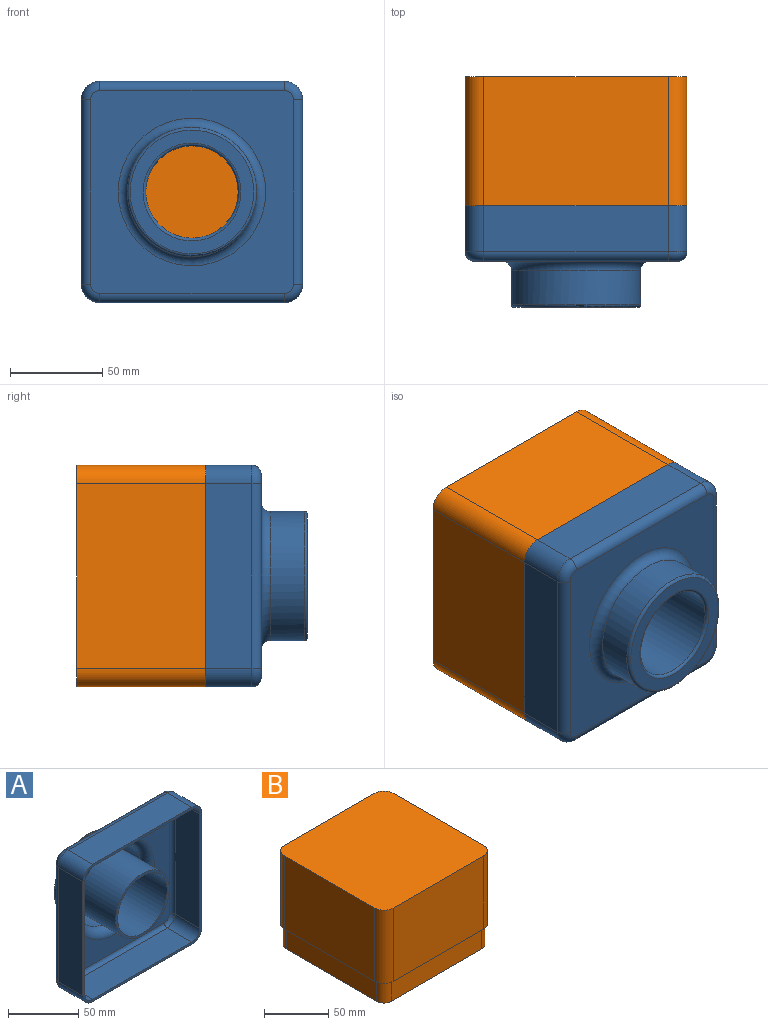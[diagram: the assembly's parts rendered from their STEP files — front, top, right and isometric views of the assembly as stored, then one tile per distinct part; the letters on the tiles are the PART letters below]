
ASSEMBLY  parts=2 mates=1
PART A: 46 faces, bbox 121.6x55x121.6 mm
  f0: plane 120x120mm, normal (0,-1,0), area 913.1mm2, adj f1,f3,f5,f6,f10,f12,f15,f21
  f1: plane 100x25mm, normal (-1,0,0), area 2500mm2, adj f0,f12,f18,f21
  f2: plane 54x54mm, normal (0,-1,0), area 326.7mm2, adj f9,f32
  f3: plane 100x25mm, normal (1,0,0), area 2500mm2, adj f0,f10,f14,f15
  f4: plane 110x110mm, normal (0,1,0), area 7052mm2, adj f11,f13,f14,f16,f17,f18,f19,f20
  f5: plane 100x25mm, normal (0,0,1), area 2500mm2, adj f0,f15,f19,f21
  f6: plane 100x25mm, normal (0,0,-1), area 2500mm2, adj f0,f10,f12,f13
  f7: cylinder r=35mm len=70mm, axis (0,-1,0), area 4068.4mm2, adj f22,f23
  f8: plane 67x67mm, normal (0,1,0), area 1319.5mm2, adj f23,f24
  f9: cylinder r=25mm len=53.5mm, axis (0,1,0), area 8403.8mm2, adj f2,f24
  f10: cylinder r=10mm len=25mm, axis (0,1,0), area 392.7mm2, adj f0,f3,f6,f11
  f11: torus R=5mm, axis (0,-1,0), area 101mm2, adj f4,f10,f13,f14
  f12: cylinder r=10mm len=25mm, axis (0,-1,0), area 392.7mm2, adj f0,f1,f6,f16
  f13: cylinder r=5mm len=100mm, axis (-1,0,0), area 785.4mm2, adj f4,f6,f11,f16
  f14: cylinder r=5mm len=100mm, axis (0,0,-1), area 785.4mm2, adj f3,f4,f11,f17
  f15: cylinder r=10mm len=25mm, axis (0,-1,0), area 392.7mm2, adj f0,f3,f5,f17
  f16: torus R=5mm, axis (0,-1,0), area 101mm2, adj f4,f12,f13,f18
  f17: torus R=5mm, axis (0,-1,0), area 101mm2, adj f4,f14,f15,f19
  f18: cylinder r=5mm len=100mm, axis (0,0,-1), area 785.4mm2, adj f1,f4,f16,f20
  f19: cylinder r=5mm len=100mm, axis (1,0,0), area 785.4mm2, adj f4,f5,f17,f20
  f20: torus R=5mm, axis (0,-1,0), area 101mm2, adj f4,f18,f19,f21
  f21: cylinder r=10mm len=25mm, axis (0,1,0), area 392.7mm2, adj f0,f1,f5,f20
  f22: torus R=40mm, axis (0,-1,0), area 1816.8mm2, adj f4,f7
  f23: torus R=33.5mm, axis (0,1,0), area 510.1mm2, adj f7,f8
  f24: torus R=26.5mm, axis (0,1,0), area 378.2mm2, adj f8,f9
  f25: plane 100x25mm, normal (1,0,0), area 2500mm2, adj f0,f35,f41,f44
  f26: plane 100x25mm, normal (-1,0,0), area 2500mm2, adj f0,f33,f37,f38
  f27: plane 110x110mm, normal (0,-1,0), area 7052mm2, adj f34,f36,f37,f39,f40,f41,f42,f43
  f28: plane 100x25mm, normal (0,0,-1), area 2500mm2, adj f0,f38,f42,f44
  f29: plane 100x25mm, normal (0,0,1), area 2500mm2, adj f0,f33,f35,f36
  f30: cylinder r=33mm len=66mm, axis (0,-1,0), area 3732.2mm2, adj f31,f45
  f31: plane 66x66mm, normal (0,-1,0), area 1131mm2, adj f30,f32
  f32: cylinder r=27mm len=54mm, axis (0,1,0), area 8991.2mm2, adj f2,f31
  f33: cylinder r=8mm len=25mm, axis (0,1,0), area 314.2mm2, adj f0,f26,f29,f34
  f34: torus R=5mm, axis (0,-1,0), area 51.1mm2, adj f27,f33,f36,f37
  f35: cylinder r=8mm len=25mm, axis (0,-1,0), area 314.2mm2, adj f0,f25,f29,f39
  f36: cylinder r=3mm len=100mm, axis (-1,0,0), area 471.2mm2, adj f27,f29,f34,f39
  f37: cylinder r=3mm len=100mm, axis (0,0,-1), area 471.2mm2, adj f26,f27,f34,f40
  f38: cylinder r=8mm len=25mm, axis (0,-1,0), area 314.2mm2, adj f0,f26,f28,f40
  f39: torus R=5mm, axis (0,-1,0), area 51.1mm2, adj f27,f35,f36,f41
  f40: torus R=5mm, axis (0,-1,0), area 51.1mm2, adj f27,f37,f38,f42
  f41: cylinder r=3mm len=100mm, axis (0,0,-1), area 471.2mm2, adj f25,f27,f39,f43
  f42: cylinder r=3mm len=100mm, axis (1,0,0), area 471.2mm2, adj f27,f28,f40,f43
  f43: torus R=5mm, axis (0,-1,0), area 51.1mm2, adj f27,f41,f42,f44
  f44: cylinder r=8mm len=25mm, axis (0,1,0), area 314.2mm2, adj f0,f25,f28,f43
  f45: torus R=40mm, axis (0,-1,0), area 2455.6mm2, adj f27,f30
PART B: 28 faces, bbox 120x120x90 mm
  f0: plane 116.19x116.19mm, normal (0,0,-1), area 930.8mm2, adj f1,f2,f3,f4,f6,f7,f8,f9
  f1: plane 100x86mm, normal (0,-1,0), area 8600mm2, adj f0,f5,f6,f9
  f2: plane 100x86mm, normal (1,0,0), area 8600mm2, adj f0,f5,f6,f7
  f3: plane 100x86mm, normal (0,1,0), area 8600mm2, adj f0,f5,f7,f8
  f4: plane 100x86mm, normal (-1,0,0), area 8600mm2, adj f0,f5,f8,f9
  f5: plane 112x112mm, normal (0,0,-1), area 12513.1mm2, adj f1,f2,f3,f4,f6,f7,f8,f9
  f6: cylinder r=6mm len=86mm, axis (0,0,1), area 810.5mm2, adj f0,f1,f2,f5
  f7: cylinder r=6mm len=86mm, axis (0,0,-1), area 810.5mm2, adj f0,f2,f3,f5
  f8: cylinder r=6mm len=86mm, axis (0,0,1), area 810.5mm2, adj f0,f3,f4,f5
  f9: cylinder r=6mm len=86mm, axis (0,0,-1), area 810.5mm2, adj f0,f1,f4,f5
  f10: cylinder r=8.1mm len=20mm, axis (0,0,-1), area 254.3mm2, adj f0,f11,f17,f18
  f11: plane 100x20mm, normal (-1,0,0), area 2000mm2, adj f0,f10,f12,f18
  f12: cylinder r=8.1mm len=20mm, axis (0,0,-1), area 254.3mm2, adj f0,f11,f13,f18
  f13: plane 100x20mm, normal (0,-1,0), area 2000mm2, adj f0,f12,f14,f18
  f14: cylinder r=8.1mm len=20mm, axis (0,0,-1), area 254.3mm2, adj f0,f13,f15,f18
  f15: plane 100x20mm, normal (1,0,0), area 2000mm2, adj f0,f14,f16,f18
  f16: cylinder r=8.1mm len=20mm, axis (0,0,-1), area 254.3mm2, adj f0,f15,f17,f18
  f17: plane 100x20mm, normal (0,1,0), area 2000mm2, adj f0,f10,f16,f18
  f18: plane 120x120mm, normal (0,0,-1), area 870.3mm2, adj f10,f11,f12,f13,f14,f15,f16,f17
  f19: plane 120x120mm, normal (0,0,1), area 14314.2mm2, adj f20,f21,f22,f23,f24,f25,f26,f27
  f20: cylinder r=10mm len=70mm, axis (0,0,1), area 1099.6mm2, adj f18,f19,f22,f24
  f21: cylinder r=10mm len=70mm, axis (0,0,-1), area 1099.6mm2, adj f18,f19,f22,f27
  f22: plane 100x70mm, normal (1,0,0), area 7000mm2, adj f18,f19,f20,f21
  f23: cylinder r=10mm len=70mm, axis (0,0,-1), area 1099.6mm2, adj f18,f19,f24,f26
  f24: plane 100x70mm, normal (0,-1,0), area 7000mm2, adj f18,f19,f20,f23
  f25: cylinder r=10mm len=70mm, axis (0,0,1), area 1099.6mm2, adj f18,f19,f26,f27
  f26: plane 100x70mm, normal (-1,0,0), area 7000mm2, adj f18,f19,f23,f25
  f27: plane 100x70mm, normal (0,1,0), area 7000mm2, adj f18,f19,f21,f25
PLACE A rot(axis=(0,0,-1),180deg) t=(-10.66,-90.92,4.02)mm
PLACE B rot(axis=(-1,0,0),90deg) t=(-10.66,-95.92,64.02)mm
MATE fastened B.f18 <-> A.f0  axis (0,-1,0) through (39.34,-75.92,124.02)mm
